# Revit family: Countertop_noSink
name_source: partatom
category: Casework
units: mm (PartAtom-declared; Revit-internal decimal feet)

## family parameters
Always vertical = Yes
Classification Number = 23.40.70.17.21.11
Cut with Voids When Loaded = No
Room Calculation Point = No
Shared = No
Work Plane-Based = No

## types (3) — shared parameters
Assembly Code = C1030400
Backsplash Height = 0' - 4"
Construction Details = http://www.arcat.com
Cost = 959.5 $
Counter Depth = 2' - 1"
Countertop Color = Counter Finish - Custom Color
Countertop Material = Counter Material - Granite
Default Elevation = 0' - 0"
Description = Linear Countertop
Edge Cost_per Inch = 1
Edge Length = 6' - 0"
Edge Type = Bevel : 1/2"
Expected Lifespan (Years) = 30
Green Building-LEED = http://www.arcat.com
Keynote = 06415
Maintenance Schedule (Months) = 12
Manufacturer = Generic
Manufacturer Fax = (203) 939-2444
Manufacturer Website = http://www.arcat.com
Model = Generic
Product Data = http://www.arcat.com
Product Properties = http://www.arcat.com
Specification = http://www.arcat.com
Sqft Cost = 71
Surface Area = 12.5 SF
Surface Thickness = 0' - 2"
Warranty Duration (Years) = 15
Width = 6' - 0"

## per-type parameters (varying)
| type | Backsplash |
| Counter_Only | No |
| Counter_ w/Back | Yes |
| Counter w/ Back-Sides | Yes |

## geometry (parser evidence)
native form markers: Sweep x4
no freeform markers — native parametric forms only
